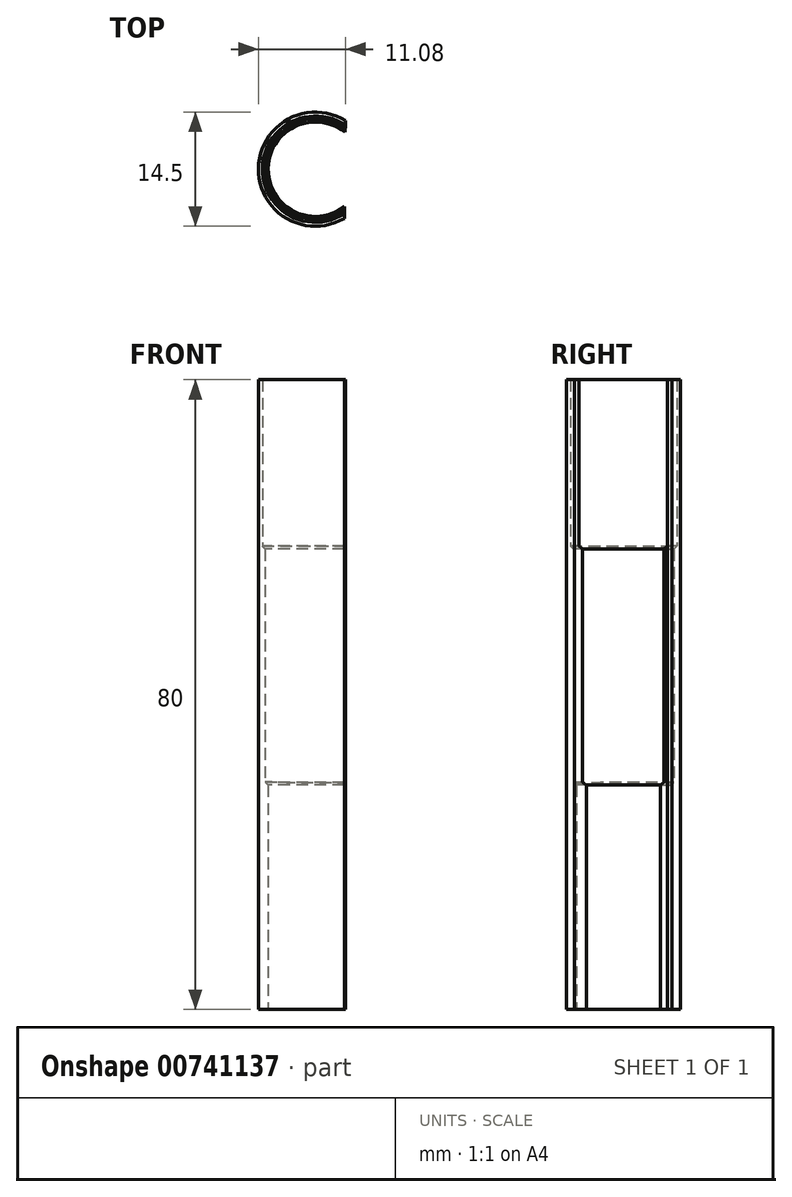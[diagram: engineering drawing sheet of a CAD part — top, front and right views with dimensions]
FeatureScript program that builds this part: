
annotation { "Feature Type Name" : "Feature", "Feature Type Description" : "" }
export const myFeature = defineFeature(function(context is Context, id is Id, definition is map)
    precondition{}
    {
        {
            var Q0;
            Q0=qCreatedBy(makeId("Top.planeOp"),FACE);
            var sketch = newSketch(context, id + "F0", { "sketchPlane" : qUnion([Q0])});
            skArc(sketch, "E0", {"start": v(3.81, 5.57) * mm, "mid": v(-6.75, 0.08) * mm, "end": v(3.67, -5.66) * mm});
            skArc(sketch, "E1", {"start": v(3.83, 6.16) * mm, "mid": v(-7.25, 0.1) * mm, "end": v(3.67, -6.25) * mm});
            skArc(sketch, "E2", {"start": v(3.75, 4.68) * mm, "mid": v(-6, 0.05) * mm, "end": v(3.67, -4.74) * mm});
            skLineSegment(sketch, "E3", {"start": v(3.67, -4.74) * mm, "end": v(3.67, -5.66) * mm});
            skLineSegment(sketch, "E4", {"start": v(3.67, -6.25) * mm, "end": v(3.67, -5.66) * mm});
            skLineSegment(sketch, "E5", {"start": v(3.75, 4.68) * mm, "end": v(3.81, 5.57) * mm});
            skLineSegment(sketch, "E6", {"start": v(3.83, 6.16) * mm, "end": v(3.81, 5.57) * mm});
            skArc(sketch, "E7", {"start": v(3.78, 5.13) * mm, "mid": v(-6.38, 0.07) * mm, "end": v(3.67, -5.2) * mm});
            skSolve(sketch);
        }
        {
            var Q0;
            Q0=makeQuery(id+"F0.imprint","IMPRINT",FACE,{"disambiguationData":[TD([[makeQuery(id+"F0.imprint","IMPRINT",EDGE,{"derivedFrom":sQuery(id+"F0.wireOp",EDGE,"E0")}),-1.0]])]});
            extrude(context, id + "F1", {"entities" : qUnion([Q0]), "depth" : 80 * mm, "offsetDistance" : 25 * mm});
        }
        {
            var Q0;
            {var subQ0=sQuery(id+"F0.wireOp",EDGE,"E0");Q0=makeQuery(id+"F0.imprint","IMPRINT",FACE,{"disambiguationData":[TD([[makeQuery(id+"F0.imprint","IMPRINT",EDGE,{"derivedFrom":subQ0}),1.0]])]});}
            extrude(context, id + "F2", {"entities" : qUnion([Q0]), "operationType" : NewBodyOperationType.ADD, "depth" : 60 * mm, "offsetDistance" : 25 * mm});
        }
        {
            var Q0;
            {var subQ0=sQuery(id+"F0.wireOp",EDGE,"E2");Q0=makeQuery(id+"F0.imprint","IMPRINT",FACE,{"disambiguationData":[TD([[makeQuery(id+"F0.imprint","IMPRINT",EDGE,{"derivedFrom":subQ0}),-1.0]])]});}
            extrude(context, id + "F3", {"entities" : qUnion([Q0]), "operationType" : NewBodyOperationType.ADD, "depth" : 30 * mm, "offsetDistance" : 25 * mm});
        }
        {
            var Q0;
            Q0=makeQuery(id+"F2.opExtrude","CAP_EDGE",EDGE,{"disambiguationData":[OSD([sQuery(id+"F0.wireOp",EDGE,"E7")])],"isStart":false});
            var Q1;
            Q1=makeQuery(id+"F3.opExtrude","CAP_EDGE",EDGE,{"disambiguationData":[OSD([sQuery(id+"F0.wireOp",EDGE,"E2")])],"isStart":false});
            chamfer(context, id + "F4", {"entities" : qUnion([Q0, Q1]), "width" : 1.5 * mm, "tangentPropagation" : true});
        }
    });
